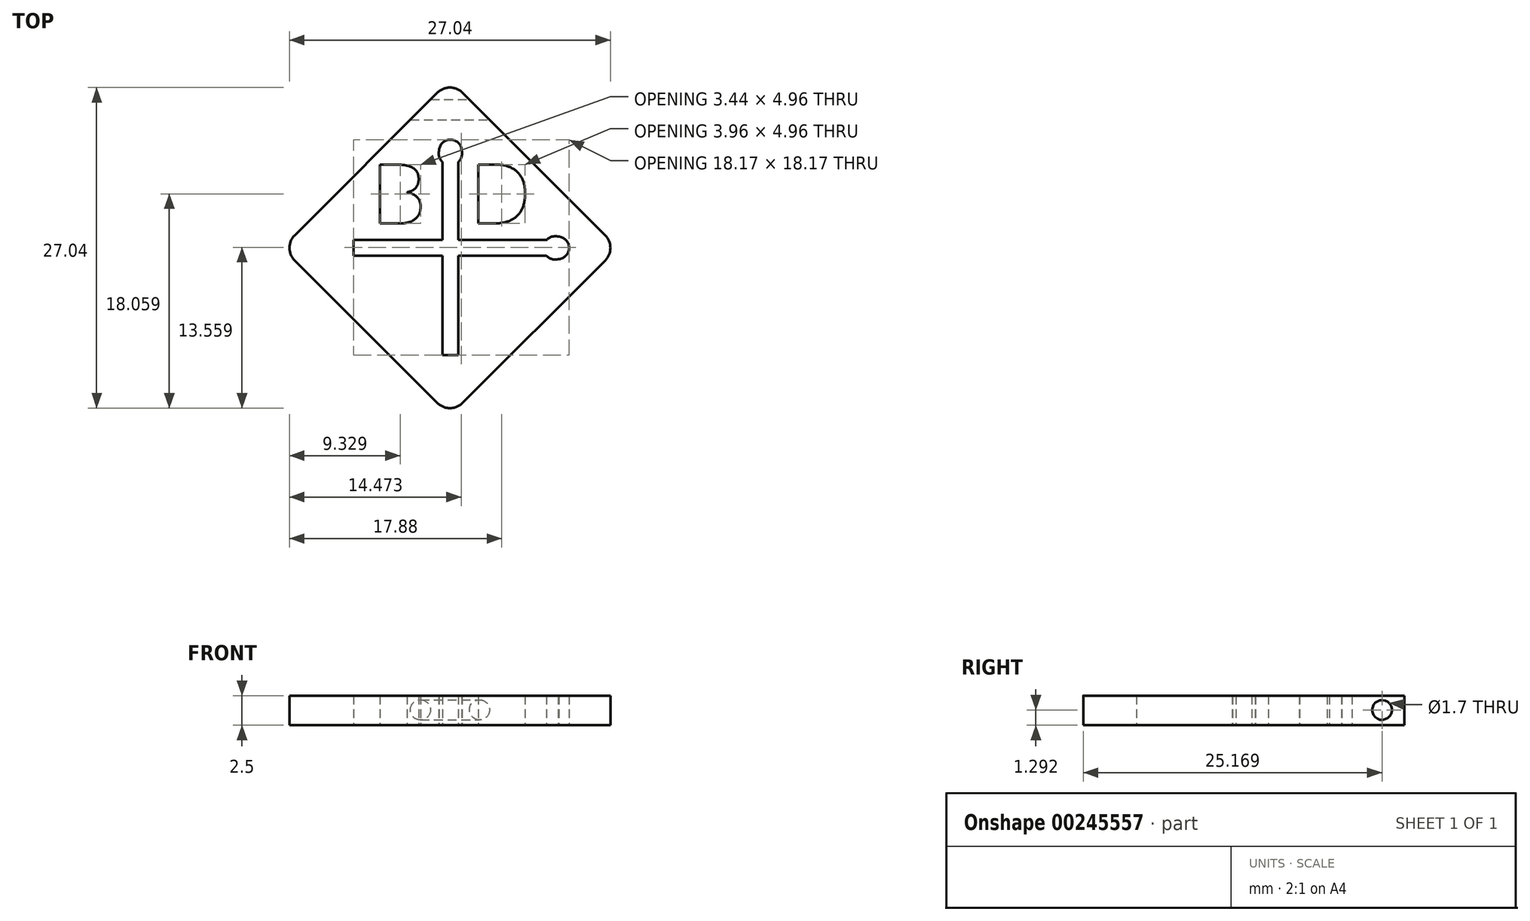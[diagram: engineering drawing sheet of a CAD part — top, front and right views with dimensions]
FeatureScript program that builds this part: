
annotation { "Feature Type Name" : "Feature", "Feature Type Description" : "" }
export const myFeature = defineFeature(function(context is Context, id is Id, definition is map)
    precondition{}
    {
        {
            var Q0;
            Q0=qCreatedBy(makeId("Top.planeOp"),FACE);
            var sketch = newSketch(context, id + "F0", { "sketchPlane" : qUnion([Q0])});
            skLineSegment(sketch, "E0", {"start": v(1.06, -1.06) * mm, "end": v(13.08, -13.08) * mm});
            skLineSegment(sketch, "E1", {"start": v(13.08, -15.2) * mm, "end": v(1.06, -27.22) * mm});
            skLineSegment(sketch, "E2", {"start": v(-1.06, -27.22) * mm, "end": v(-13.08, -15.2) * mm});
            skLineSegment(sketch, "E3", {"start": v(-13.08, -13.08) * mm, "end": v(-1.06, -1.06) * mm});
            skPoint(sketch, "E4.visualSharp", {"position": v(0, 0) * mm});
            skArc(sketch, "E4.filletArc", {"start": v(1.06, -1.06) * mm, "mid": v(0, -0.62) * mm, "end": v(-1.06, -1.06) * mm});
            skPoint(sketch, "E5.visualSharp", {"position": v(-14.14, -14.14) * mm});
            skArc(sketch, "E5.filletArc", {"start": v(-13.08, -13.08) * mm, "mid": v(-13.52, -14.14) * mm, "end": v(-13.08, -15.2) * mm});
            skPoint(sketch, "E6.visualSharp", {"position": v(14.14, -14.14) * mm});
            skArc(sketch, "E6.filletArc", {"start": v(13.08, -15.2) * mm, "mid": v(13.52, -14.14) * mm, "end": v(13.08, -13.08) * mm});
            skPoint(sketch, "E7.visualSharp", {"position": v(0, -28.28) * mm});
            skArc(sketch, "E7.filletArc", {"start": v(-1.06, -27.22) * mm, "mid": v(0, -27.66) * mm, "end": v(1.06, -27.22) * mm});
            skLineSegment(sketch, "E8", {"start": v(0, 0) * mm, "end": v(0, -31.86) * mm, "construction": true});
            skLineSegment(sketch, "E9", {"start": v(-14.14, -14.14) * mm, "end": v(14.14, -14.14) * mm, "construction": true});
            skLineSegment(sketch, "E10", {"start": v(-8.13, -13.48) * mm, "end": v(-8.13, -14.8) * mm});
            skLineSegment(sketch, "E11", {"start": v(-8.13, -14.8) * mm, "end": v(8.13, -14.8) * mm});
            skLineSegment(sketch, "E12", {"start": v(8.13, -13.48) * mm, "end": v(-8.13, -13.48) * mm});
            skLineSegment(sketch, "E13", {"start": v(-8.13, -13.48) * mm, "end": v(0, -13.48) * mm, "construction": true});
            skLineSegment(sketch, "E14", {"start": v(0, -13.48) * mm, "end": v(8.13, -13.48) * mm, "construction": true});
            skArc(sketch, "E15", {"start": v(9.18, -15.1) * mm, "mid": v(10.04, -14.12) * mm, "end": v(9.13, -13.2) * mm});
            skArc(sketch, "E16", {"start": v(9.13, -13.2) * mm, "mid": v(8.6, -13.2) * mm, "end": v(8.13, -13.48) * mm});
            skArc(sketch, "E17", {"start": v(8.13, -14.8) * mm, "mid": v(8.61, -15.1) * mm, "end": v(9.18, -15.1) * mm});
            skLineSegment(sketch, "E18", {"start": v(-0.62, -23.19) * mm, "end": v(0.7, -23.19) * mm});
            skLineSegment(sketch, "E19", {"start": v(0.7, -23.19) * mm, "end": v(0.7, -6.92) * mm});
            skLineSegment(sketch, "E20", {"start": v(-0.62, -6.92) * mm, "end": v(-0.62, -23.19) * mm});
            skLineSegment(sketch, "E21", {"start": v(-0.62, -23.19) * mm, "end": v(-0.62, -15.05) * mm, "construction": true});
            skLineSegment(sketch, "E22", {"start": v(-0.62, -15.05) * mm, "end": v(-0.62, -6.92) * mm, "construction": true});
            skArc(sketch, "E23", {"start": v(0.99, -5.88) * mm, "mid": v(0.02, -5.01) * mm, "end": v(-0.91, -5.92) * mm});
            skArc(sketch, "E24", {"start": v(-0.91, -5.92) * mm, "mid": v(-0.9, -6.46) * mm, "end": v(-0.62, -6.92) * mm});
            skArc(sketch, "E25", {"start": v(0.7, -6.92) * mm, "mid": v(1, -6.44) * mm, "end": v(0.99, -5.88) * mm});
            skText(sketch, "E26", { "text": "B\n", "fontName": "OpenSans-Regular.ttf"});
            skText(sketch, "E27", { "text": "D", "fontName": "OpenSans-Regular.ttf"});
            const initialGuessF0  = {"E26": [-0.00659, -0.01208, 1, 0, 0.005], "E27": [0.0017, -0.01208, 1, 0, 0.005]};
            skSetInitialGuess(sketch, initialGuessF0);
            skSolve(sketch);
        }
        {
            var Q0;
            Q0=makeQuery(id+"F0.imprint","IMPRINT",FACE,{"disambiguationData":[TD([[makeQuery(id+"F0.imprint","IMPRINT",EDGE,{"derivedFrom":sQuery(id+"F0.wireOp",EDGE,"E0")}),-1.0]])]});
            extrude(context, id + "F1", {"entities" : qUnion([Q0]), "depth" : 2.5 * mm});
        }
        {
            var Q0;
            Q0=qCreatedBy(makeId("Right.planeOp"),FACE);
            var sketch = newSketch(context, id + "F2", { "sketchPlane" : qUnion([Q0])});
            skCircle(sketch, "E28", {"center": v(-2.5, 1.3) * mm, "radius": 0.85 * mm});
            skSolve(sketch);
        }
        {
            var Q0;
            Q0=qSketchRegion(id+"F2",true);
            extrude(context, id + "F3", {"entities" : qUnion([Q0]), "operationType" : NewBodyOperationType.REMOVE, "endBound" : BoundingType.SYMMETRIC, "oppositeDirection" : true, "depth" : 25 * mm});
        }
    });
